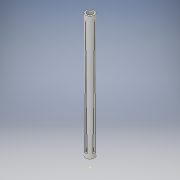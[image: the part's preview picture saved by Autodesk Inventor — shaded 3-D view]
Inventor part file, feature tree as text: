
AUTODESK INVENTOR PART (.ipt)
format: ipt  version: 2019 (Build 230136000, 136)  size: 150,016 bytes
history: native  units: mm
features: sketch x11, extrude x10, plane x2
ambient origin geometry x8: Origin, YZ Plane, XZ Plane, XY Plane, X Axis, Y Axis, Z Axis, Center Point
bodies: Solid1 (feature_tree)
feature tree (23):
  extrude  "Extrusion1"  Depth=500.0mm TaperAngle=0.0deg
  plane  "Work Plane1"
  extrude  "Extrusion2"  Depth=15.0mm
  plane  "Work Plane2"
  extrude  "Extrusion3"  Depth=15.0mm
  extrude  "Extrusion4"  Depth=500.0mm TaperAngle=0.0deg
  extrude  "Extrusion5"  Depth=500.0mm TaperAngle=0.0deg
  extrude  "Extrusion6"  Depth=10.0mm TaperAngle=0.0deg
  sketch  "Sketch7"  dims[d18=10.0mm d19=0.0mm d20=10.0mm d21=0.0mm]
  extrude  "Extrusion7"  Depth=10.0mm TaperAngle=0.0deg
  extrude  "Extrusion8"  Depth=15.0mm TaperAngle=0.0deg
  extrude  "Extrusion9"  [1 undecoded]
  extrude  "Extrusion10"  [1 undecoded]
  sketch  "Sketch1"  dims[d0=30.0mm d1=500.0mm d2=0.0mm]
  sketch  "Sketch2"  dims[d3=15.0mm d4=9.425mm]
  sketch  "Sketch3"  dims[d5=500.0mm d6=0.0mm d7=15.0mm]
  sketch  "Sketch4"  dims[d8=9.425mm d9=500.0mm d10=0.0mm]
  sketch  "Sketch5"  dims[d11=20.0mm d12=500.0mm d13=0.0mm]
  sketch  "Sketch6"  dims[d14=10.0mm d15=0.0mm d16=10.0mm d17=0.0mm]
  sketch  "Sketch8"  dims[d22=15.0mm d23=0.0mm d24=15.0mm d25=0.0mm]
  sketch  "Sketch9"
  sketch  "Sketch10"
  sketch  "Sketch11"
note: 2 required parameter values undecoded (feature->parameter linkage not recoverable at this tier; creation-order binding heuristic only, values carry confidence <= 0.55)
